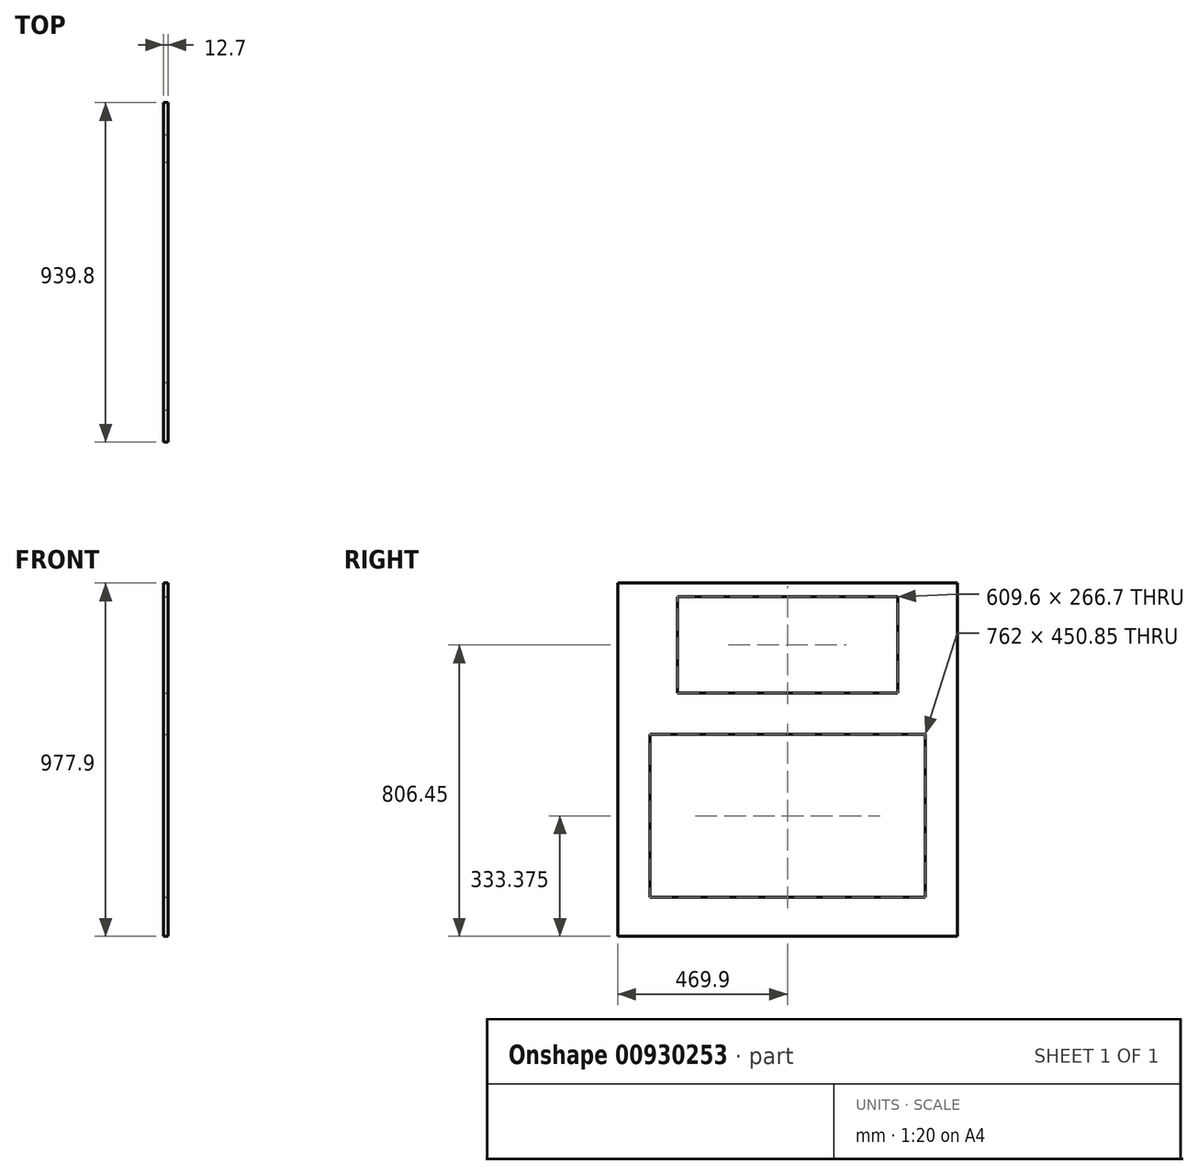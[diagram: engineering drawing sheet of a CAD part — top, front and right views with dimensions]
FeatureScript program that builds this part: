
annotation { "Feature Type Name" : "Feature", "Feature Type Description" : "" }
export const myFeature = defineFeature(function(context is Context, id is Id, definition is map)
    precondition{}
    {
        {
            var Q0;
            Q0=qCreatedBy(makeId("Right.planeOp"),FACE);
            var sketch = newSketch(context, id + "F0", { "sketchPlane" : qUnion([Q0])});
            skLineSegment(sketch, "E0.bottom", {"start": v(469.9, -488.95) * mm, "end": v(-469.9, -488.95) * mm});
            skLineSegment(sketch, "E0.top", {"start": v(469.9, 488.95) * mm, "end": v(-469.9, 488.95) * mm});
            skLineSegment(sketch, "E0.left", {"start": v(469.9, -488.95) * mm, "end": v(469.9, 488.95) * mm});
            skLineSegment(sketch, "E0.right", {"start": v(-469.9, -488.95) * mm, "end": v(-469.9, 488.95) * mm});
            skPoint(sketch, "E0.middle", {"position": v(0, 0) * mm});
            skSolve(sketch);
        }
        {
            var Q0;
            Q0=qSketchRegion(id+"F0",true);
            extrude(context, id + "F1", {"entities" : qUnion([Q0]), "endBound" : BoundingType.SYMMETRIC, "depth" : 12.7 * mm});
        }
        {
            var Q0;
            Q0=makeQuery(id+"F1.opExtrude","CAP_FACE",FACE,{"disambiguationData":[OSD([sQuery(id+"F0.wireOp",EDGE,"E0.bottom"),sQuery(id+"F0.wireOp",EDGE,"E0.top"),sQuery(id+"F0.wireOp",EDGE,"E0.left"),sQuery(id+"F0.wireOp",EDGE,"E0.right")])],"isStart":false});
            var sketch = newSketch(context, id + "F2", { "sketchPlane" : qUnion([Q0])});
            skLineSegment(sketch, "E1.bottom", {"start": v(-381, 69.85) * mm, "end": v(381, 69.85) * mm});
            skLineSegment(sketch, "E1.top", {"start": v(-381, -381) * mm, "end": v(381, -381) * mm});
            skLineSegment(sketch, "E1.left", {"start": v(-381, 69.85) * mm, "end": v(-381, -381) * mm});
            skLineSegment(sketch, "E1.right", {"start": v(381, 69.85) * mm, "end": v(381, -381) * mm});
            skLineSegment(sketch, "E2.bottom", {"start": v(-304.8, 450.85) * mm, "end": v(304.8, 450.85) * mm});
            skLineSegment(sketch, "E2.top", {"start": v(-304.8, 184.15) * mm, "end": v(304.8, 184.15) * mm});
            skLineSegment(sketch, "E2.left", {"start": v(-304.8, 450.85) * mm, "end": v(-304.8, 184.15) * mm});
            skLineSegment(sketch, "E2.right", {"start": v(304.8, 450.85) * mm, "end": v(304.8, 184.15) * mm});
            skLineSegment(sketch, "E3", {"start": v(0, -488.95) * mm, "end": v(0, -381) * mm, "construction": true});
            skLineSegment(sketch, "E4", {"start": v(0, 450.85) * mm, "end": v(0, 488.95) * mm, "construction": true});
            skSolve(sketch);
        }
        {
            var Q0;
            Q0=qSketchRegion(id+"F2",true);
            extrude(context, id + "F3", {"entities" : qUnion([Q0]), "operationType" : NewBodyOperationType.REMOVE, "endBound" : BoundingType.THROUGH_ALL, "oppositeDirection" : true, "depth" : 25.4 * mm});
        }
    });
